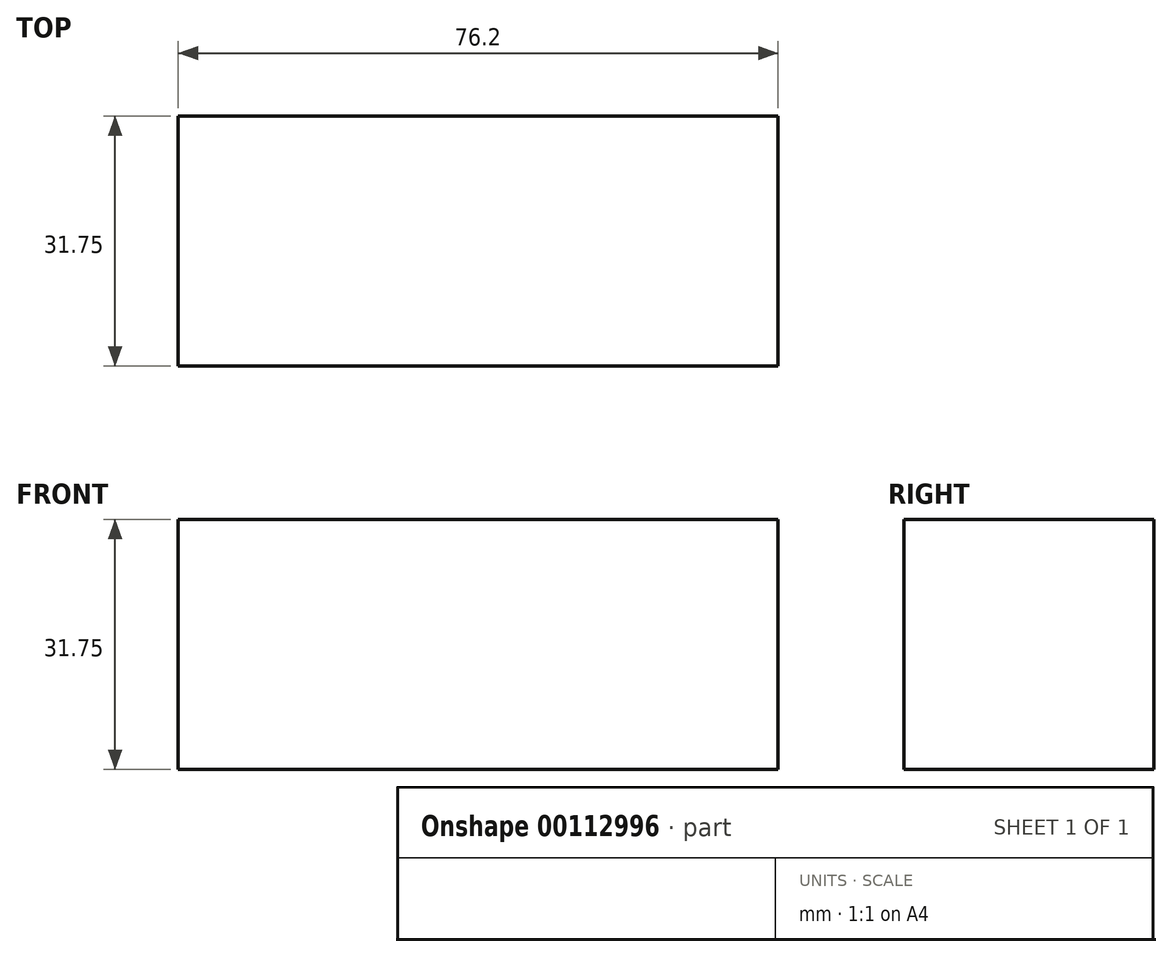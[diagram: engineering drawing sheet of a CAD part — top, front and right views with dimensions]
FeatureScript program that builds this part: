
annotation { "Feature Type Name" : "Feature", "Feature Type Description" : "" }
export const myFeature = defineFeature(function(context is Context, id is Id, definition is map)
    precondition{}
    {
        {
            var Q0;
            Q0=qCreatedBy(makeId("Top.planeOp"),FACE);
            var sketch = newSketch(context, id + "F0", { "sketchPlane" : qUnion([Q0])});
            skLineSegment(sketch, "E0.bottom", {"start": v(-25.92, 12.73) * mm, "end": v(50.28, 12.73) * mm});
            skLineSegment(sketch, "E0.top", {"start": v(-25.92, -19.02) * mm, "end": v(50.28, -19.02) * mm});
            skLineSegment(sketch, "E0.left", {"start": v(-25.92, 12.73) * mm, "end": v(-25.92, -19.02) * mm});
            skLineSegment(sketch, "E0.right", {"start": v(50.28, 12.73) * mm, "end": v(50.28, -19.02) * mm});
            skSolve(sketch);
        }
        {
            var Q0;
            Q0 = qSketchRegion(id + "F0", true);
            extrude(context, id + "F1", {"entities" : qUnion([Q0]), "depth" : 31.75 * mm});
        }
    });
